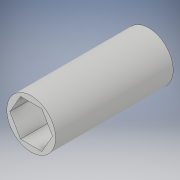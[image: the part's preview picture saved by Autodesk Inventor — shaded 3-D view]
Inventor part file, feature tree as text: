
AUTODESK INVENTOR PART (.ipt)
format: ipt  version: 2018 (Build 220112000, 112)  size: 100,352 bytes
history: native  units: in
note: dims shown in document units (in); Inventor stores cm internally (conversion verified against a paired STEP export)
features: extrude x1, sketch x1
ambient origin geometry x8: Origin, YZ Plane, XZ Plane, XY Plane, X Axis, Y Axis, Z Axis, Center Point
bodies: Solid1 (feature_tree)
feature tree (2):
  extrude  "Extrusion1"  Depth=1.59in
  sketch  "Sketch1"  dims[d0=0.5in d1=0.66in d2=1.59in d3=0.0in]
